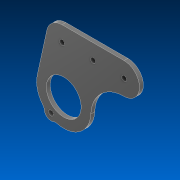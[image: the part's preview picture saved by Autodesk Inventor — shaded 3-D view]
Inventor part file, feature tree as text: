
AUTODESK INVENTOR PART (.ipt)
format: ipt  version: 2022 (Build 260153000, 153)  size: 138,752 bytes
history: native  units: in
note: dims shown in document units (in); Inventor stores cm internally (conversion verified against a paired STEP export)
features: sketch x2, extrude x1, projected_geometry x1
ambient origin geometry x8: Origin, YZ Plane, XZ Plane, XY Plane, X Axis, Y Axis, Z Axis, Center Point
bodies: Solid1 (feature_tree)
feature tree (4):
  extrude  "Extrusion1"  Depth=2.4518in
  sketch  "Sketch2"  dims[d3=1.4944in d4=0.163in d5=1.125in d6=1.75in d7=1.0in d8=0.125in d9=0.0in d10=0.25in d11=1.3in d12=0.315in]
  sketch  "Sketch1"  dims[d0=1.0in d2=2.4518in]
  projected_geometry  "Projected Loop1"
